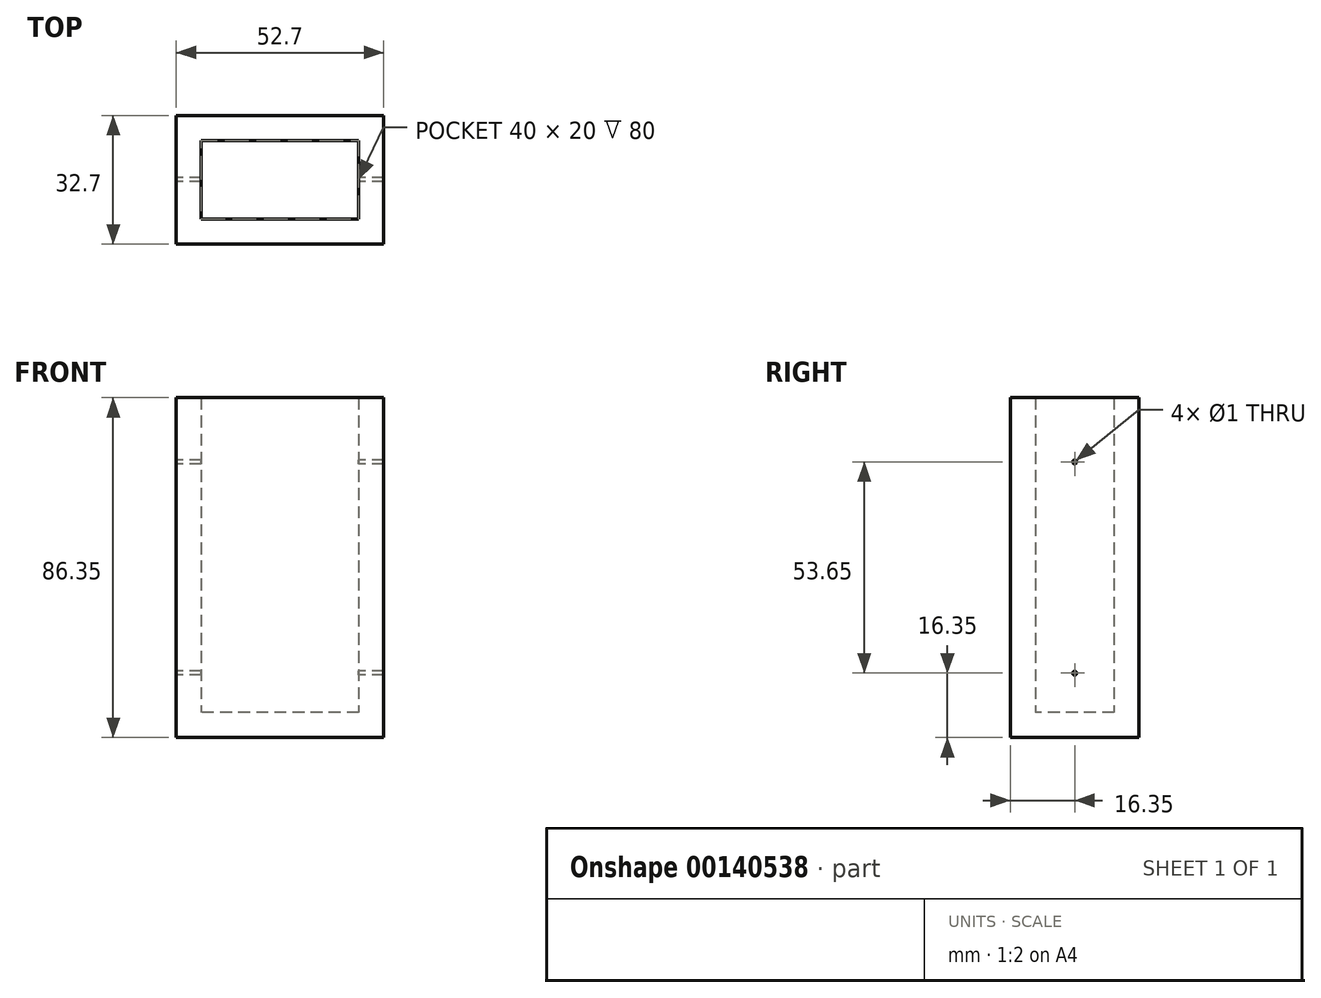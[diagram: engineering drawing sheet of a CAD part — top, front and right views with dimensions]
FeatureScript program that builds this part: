
annotation { "Feature Type Name" : "Feature", "Feature Type Description" : "" }
export const myFeature = defineFeature(function(context is Context, id is Id, definition is map)
    precondition{}
    {
        {
            var Q0;
            Q0=qCreatedBy(makeId("Top.planeOp"),FACE);
            var sketch = newSketch(context, id + "F0", { "sketchPlane" : qUnion([Q0])});
            skLineSegment(sketch, "E0.bottom", {"start": v(26.35, 16.35) * mm, "end": v(-26.35, 16.35) * mm});
            skLineSegment(sketch, "E0.top", {"start": v(26.35, -16.35) * mm, "end": v(-26.35, -16.35) * mm});
            skLineSegment(sketch, "E0.left", {"start": v(26.35, 16.35) * mm, "end": v(26.35, -16.35) * mm});
            skLineSegment(sketch, "E0.right", {"start": v(-26.35, 16.35) * mm, "end": v(-26.35, -16.35) * mm});
            skPoint(sketch, "E0.middle", {"position": v(0, 0) * mm});
            skSolve(sketch);
        }
        {
            var Q0;
            Q0 = qSketchRegion(id + "F0", true);
            extrude(context, id + "F1", {"entities" : qUnion([Q0]), "depth" : 86.35 * mm});
        }
        {
            var Q0;
            Q0=makeQuery(id+"F1.opExtrude","CAP_FACE",FACE,{"disambiguationData":[OSD([sQuery(id+"F0.wireOp",EDGE,"E0.bottom"),sQuery(id+"F0.wireOp",EDGE,"E0.top"),sQuery(id+"F0.wireOp",EDGE,"E0.left"),sQuery(id+"F0.wireOp",EDGE,"E0.right")])],"isStart":false});
            shell(context, id + "F2", {"entities" : qUnion([Q0]), "thickness" : 6.35 * mm});
        }
        {
            var Q0;
            Q0=makeQuery(id+"F1.opExtrude","SWEPT_FACE",FACE,{"disambiguationData":[OSD([sQuery(id+"F0.wireOp",EDGE,"E0.right")])]});
            var sketch = newSketch(context, id + "F3", { "sketchPlane" : qUnion([Q0])});
            skLineSegment(sketch, "E1.bottom", {"start": v(-16.35, 86.35) * mm, "end": v(0, 86.35) * mm});
            skLineSegment(sketch, "E1.top", {"start": v(-16.35, 70) * mm, "end": v(0, 70) * mm});
            skLineSegment(sketch, "E1.left", {"start": v(-16.35, 86.35) * mm, "end": v(-16.35, 70) * mm});
            skLineSegment(sketch, "E1.right", {"start": v(0, 86.35) * mm, "end": v(0, 70) * mm});
            skLineSegment(sketch, "E2.bottom", {"start": v(-16.35, 0) * mm, "end": v(0, 0) * mm});
            skLineSegment(sketch, "E2.top", {"start": v(-16.35, 16.35) * mm, "end": v(0, 16.35) * mm});
            skLineSegment(sketch, "E2.left", {"start": v(-16.35, 0) * mm, "end": v(-16.35, 16.35) * mm});
            skLineSegment(sketch, "E2.right", {"start": v(0, 0) * mm, "end": v(0, 16.35) * mm});
            skSolve(sketch);
        }
        {
            var Q0;
            Q0=sQuery(id+"F3.wireOp",VERTEX,"E1.right.end");
            var Q1;
            Q1=makeQuery(id+"F1.opExtrude","SWEPT_BODY",BODY,{"disambiguationData":[OSD([sQuery(id+"F0.wireOp",EDGE,"E0.bottom"),sQuery(id+"F0.wireOp",EDGE,"E0.top"),sQuery(id+"F0.wireOp",EDGE,"E0.left"),sQuery(id+"F0.wireOp",EDGE,"E0.right")])]});
            hole(context, id + "F4", {"style" : HoleStyle.SIMPLE, "endStyle" : HoleEndStyle.THROUGH, "holeDiameter" : 1 * mm, "locations" : qUnion([Q0]), "scope" : qUnion([Q1]), "isTappedThrough" : true});
        }
        {
            var Q0;
            Q0=sQuery(id+"F3.wireOp",VERTEX,"E2.right.end");
            var Q1;
            Q1=makeQuery(id+"F1.opExtrude","SWEPT_BODY",BODY,{"disambiguationData":[OSD([sQuery(id+"F0.wireOp",EDGE,"E0.bottom"),sQuery(id+"F0.wireOp",EDGE,"E0.top"),sQuery(id+"F0.wireOp",EDGE,"E0.left"),sQuery(id+"F0.wireOp",EDGE,"E0.right")])]});
            hole(context, id + "F5", {"style" : HoleStyle.SIMPLE, "endStyle" : HoleEndStyle.THROUGH, "holeDiameter" : 1 * mm, "locations" : qUnion([Q0]), "scope" : qUnion([Q1]), "isTappedThrough" : true});
        }
    });
